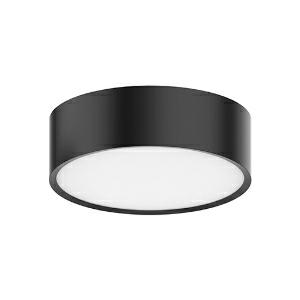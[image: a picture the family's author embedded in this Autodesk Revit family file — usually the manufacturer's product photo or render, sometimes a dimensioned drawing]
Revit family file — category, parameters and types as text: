
# Revit family: ledceilinglu-e_rd142-24w-830-bl_540001296100
name_source: partatom
category: Leuchten
revit_build: Autodesk Revit 2016 (Build: 20190508_0715(x64)
units: mm (PartAtom-declared; Revit-internal decimal feet)

## family parameters
Basisbauteil = Fläche
Beim Laden mit Abzugskörper schneiden = Nein
Bemaßung runder Anschluss = Durchmesser verwenden
Gemeinsam genutzt = Nein
Lichtquelle = Nein
Raumberechnungspunkt = Nein
Teiletyp = Normal

## types (1)
- LEDCeilingLu-E Rd142-24W-830-BL (1 x LED, 2040 lm)
    Approval mark = CE
    Beschreibung = Stylish and compact ceiling luminaire. Clean “twist-and-lock” mounting system. High quality full metal body. Low height of only 46mm. Suitable for ceiling and wall mounting.
    CIE Flux Codes = 49 79 96 100 100
    Control Gear = Electronic ballast
    Height = 100 mm  [stored 0.328084 ft]
    Hersteller = OPPLE
    Lamp Light Flux = 2040 lm
    Lamp count = 1
    Lampe = 1 x LED
    Length = 100 mm  [stored 0.328084 ft]
    Luminous efficacy = 85 lm/W
    ModVariant = Nein
    Modell = 540001296100
    Mounting Place = Wall, Ceiling
    Mounting Type = Surface mounted
    Number of Poles = 1
    OnlyDefault = Ja
    Power Factor = 1
    Product Name = LEDCeilingLu-E Rd142-24W-830-BL
    Product group = Ceiling Light Luna
    ProductGroupID = 305
    Protection Class = Protection class II
    Protection Degree = IP 20
    RLX_Detail_Level = 1
    RlxData = <blob elided: 129913 chars, md5=255bc02d>
    Scheinlast = 24 VA
    Socket = socket
    Standby Power = 0 W
    System Light Flux = 2040 lm
    System Power = 24 W
    Typenbild = luna_bl_rd142.jpg
    Typenkommentare = Product without accessories
    URL = http://relux.com
    VarID = ---
    Voltage = 230 V
    Voltage Range = 220-240 V
    Vorgabe-Ansicht = 1800 mm
    Weight = 0.00 kg
    Width = 100 mm  [stored 0.328084 ft]

note: [stored X ft] marks values corroborated as IEEE doubles in the binary element streams (Revit-internal decimal feet)

## geometry (parser evidence)
native form markers: Blend x4, Sweep x11
no freeform markers — native parametric forms only
